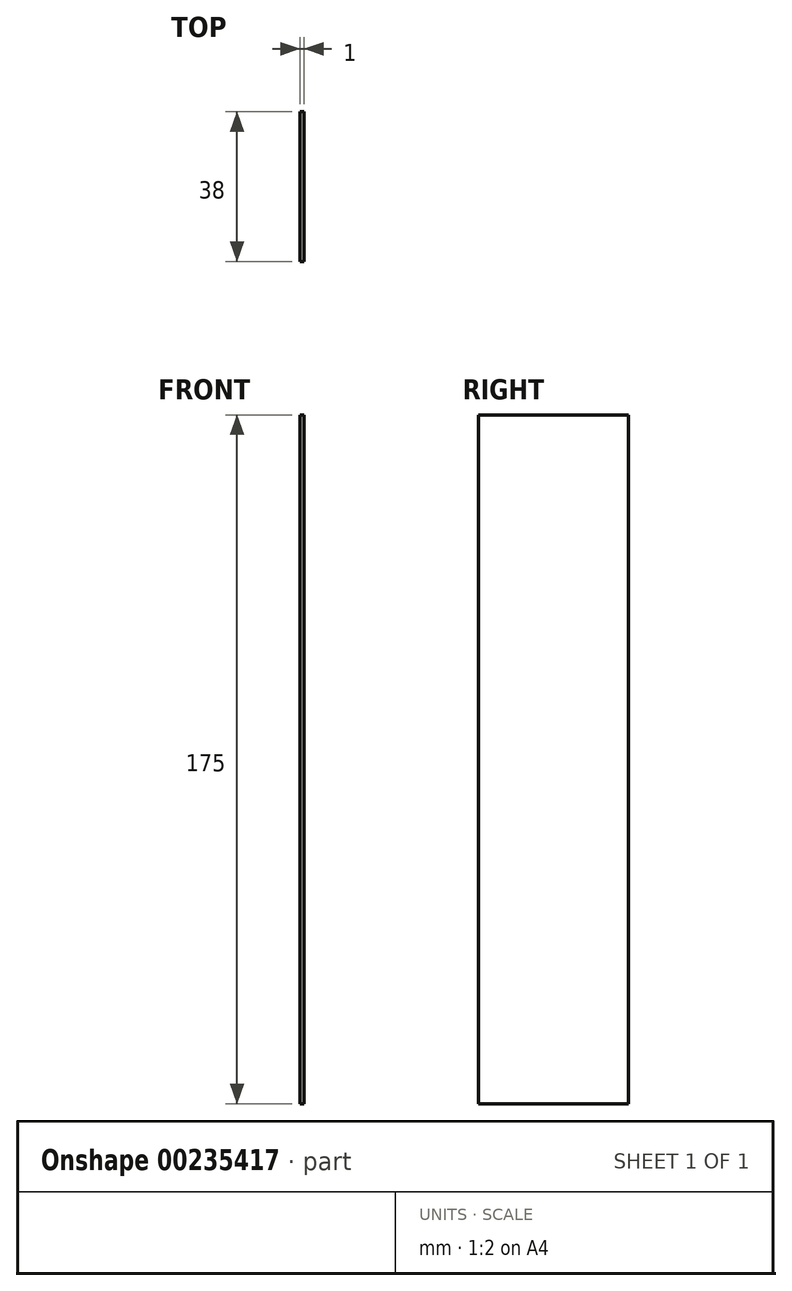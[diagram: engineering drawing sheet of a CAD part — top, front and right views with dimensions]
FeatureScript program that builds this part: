
annotation { "Feature Type Name" : "Feature", "Feature Type Description" : "" }
export const myFeature = defineFeature(function(context is Context, id is Id, definition is map)
    precondition{}
    {
        {
            var Q0;
            Q0=qCreatedBy(makeId("Right.planeOp"),FACE);
            var sketch = newSketch(context, id + "F0", { "sketchPlane" : qUnion([Q0])});
            skLineSegment(sketch, "E0.bottom", {"start": v(0, 0) * mm, "end": v(38, 0) * mm});
            skLineSegment(sketch, "E0.top", {"start": v(0, 175) * mm, "end": v(38, 175) * mm});
            skLineSegment(sketch, "E0.left", {"start": v(0, 0) * mm, "end": v(0, 175) * mm});
            skLineSegment(sketch, "E0.right", {"start": v(38, 0) * mm, "end": v(38, 175) * mm});
            skSolve(sketch);
        }
        {
            var Q0;
            Q0=makeQuery(id+"F0.imprint","IMPRINT",FACE,{"disambiguationData":[TD([[makeQuery(id+"F0.imprint","IMPRINT",EDGE,{"derivedFrom":sQuery(id+"F0.wireOp",EDGE,"E0.bottom")}),1.0]])]});
            extrude(context, id + "F1", {"entities" : qUnion([Q0]), "depth" : 1 * mm});
        }
    });
